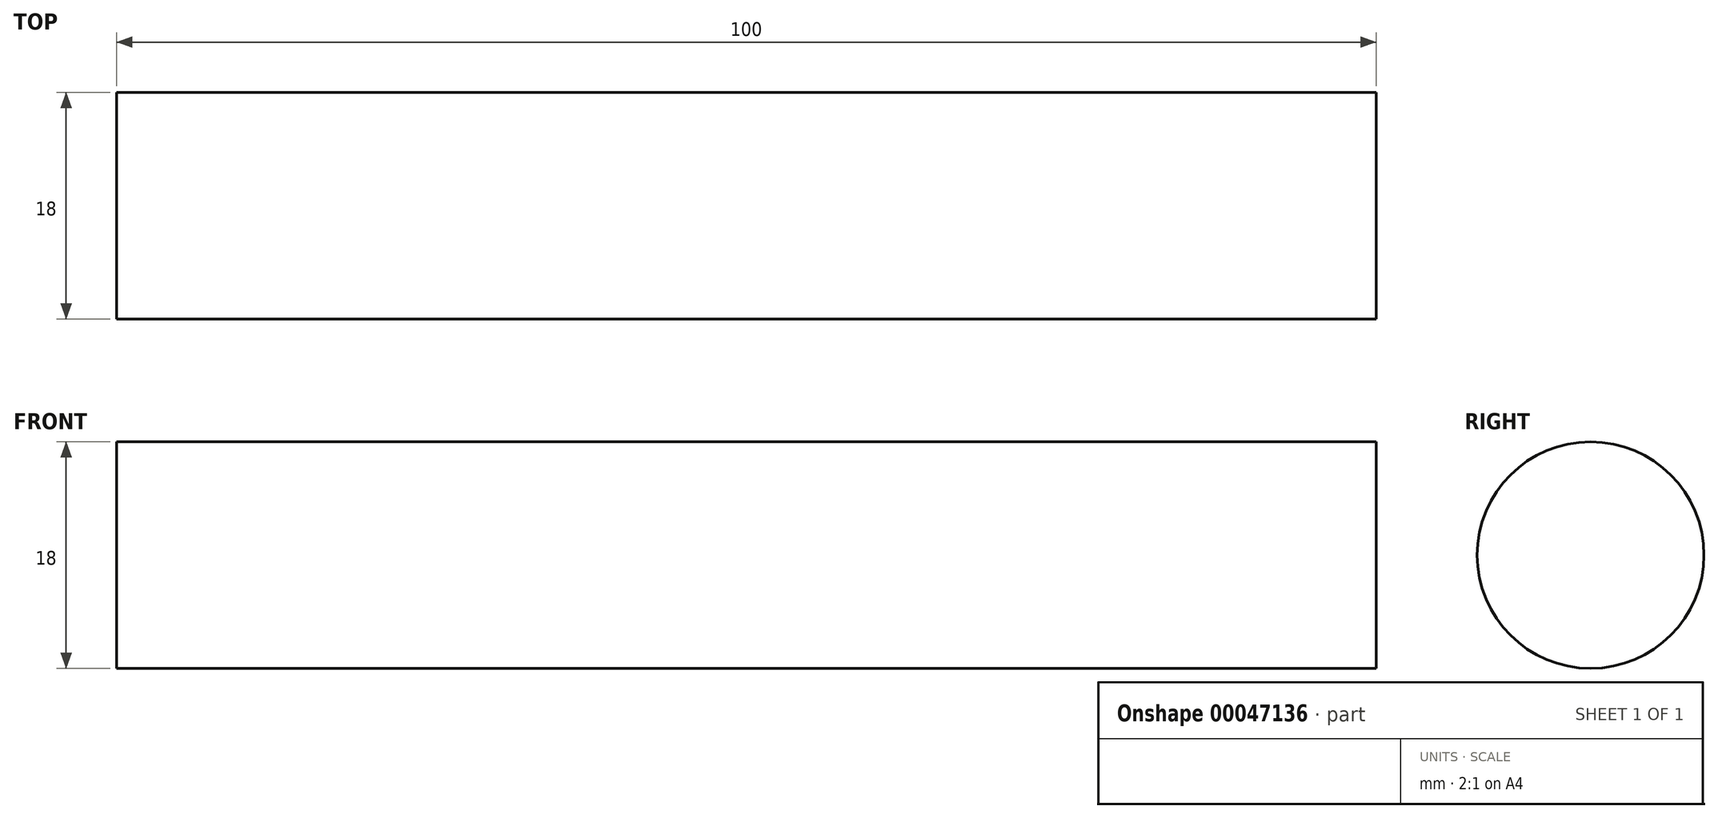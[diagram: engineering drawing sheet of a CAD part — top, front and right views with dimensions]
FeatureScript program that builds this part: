
annotation { "Feature Type Name" : "Feature", "Feature Type Description" : "" }
export const myFeature = defineFeature(function(context is Context, id is Id, definition is map)
    precondition{}
    {
        {
            var Q0;
            Q0=qCreatedBy(makeId("Right.planeOp"),FACE);
            var sketch = newSketch(context, id + "F0", { "sketchPlane" : qUnion([Q0])});
            skCircle(sketch, "E0", {"center": v(0, 0) * mm, "radius": 9 * mm});
            skSolve(sketch);
        }
        {
            var Q0;
            Q0=makeQuery(id+"F0.imprint","IMPRINT",FACE,{"disambiguationData":[TD([[makeQuery(id+"F0.imprint","IMPRINT",EDGE,{"derivedFrom":sQuery(id+"F0.wireOp",EDGE,"E0")}),1.0]])]});
            var Q1;
            Q1=sQuery(id+"F0.wireOp",EDGE,"E0");
            extrude(context, id + "F1", {"entities" : qUnion([Q0]), "surfaceEntities" : qUnion([Q1]), "endBound" : BoundingType.SYMMETRIC, "depth" : 100 * mm});
        }
    });
